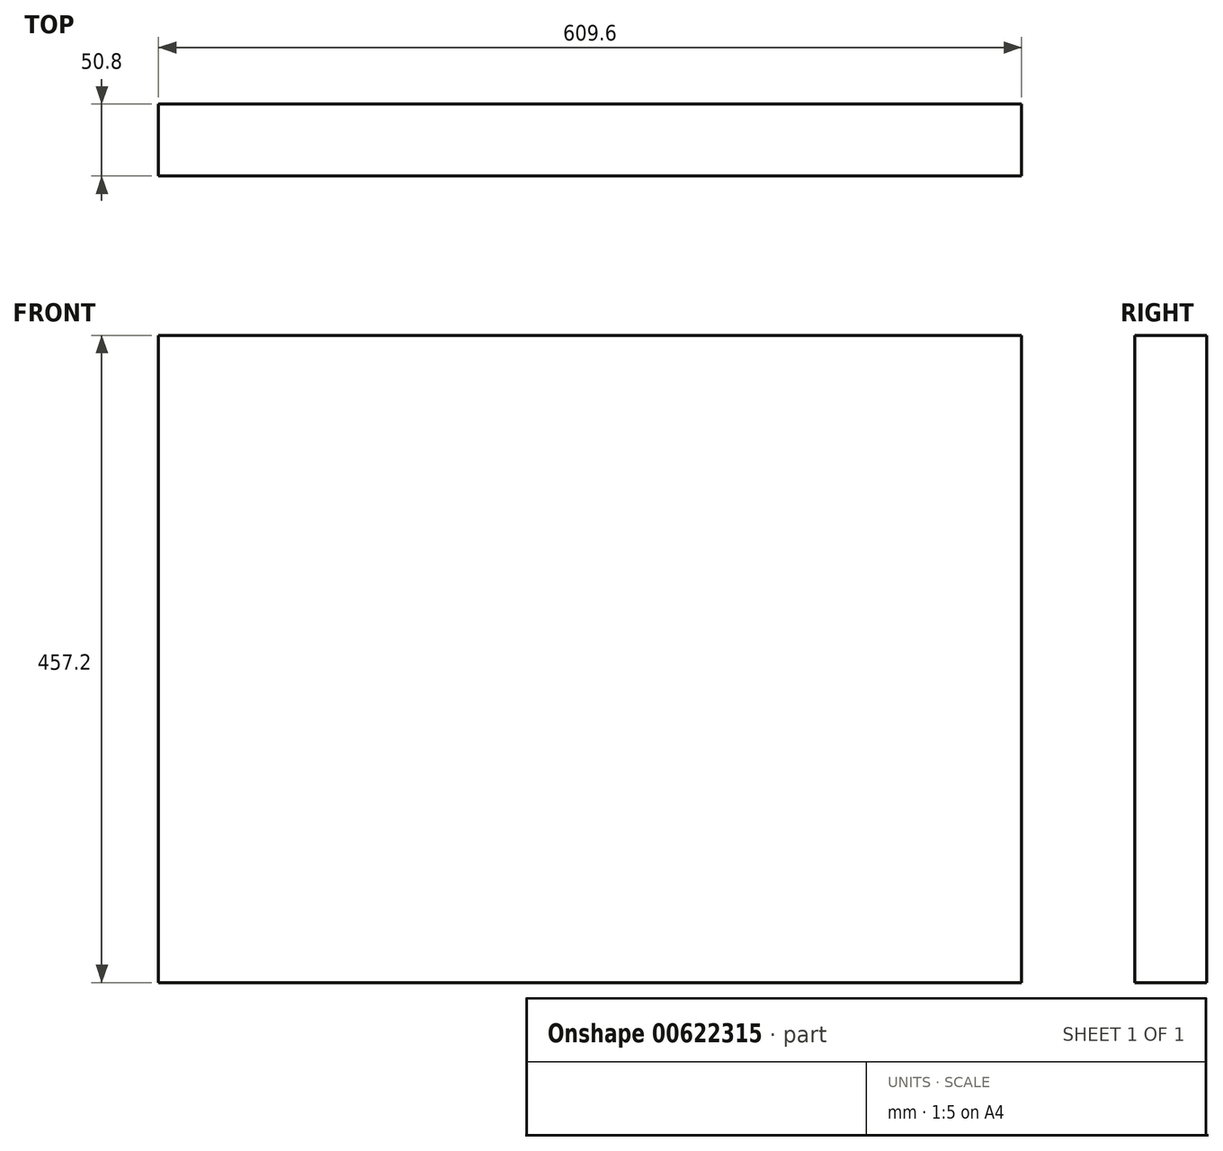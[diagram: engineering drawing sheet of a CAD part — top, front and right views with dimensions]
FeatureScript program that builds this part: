
annotation { "Feature Type Name" : "Feature", "Feature Type Description" : "" }
export const myFeature = defineFeature(function(context is Context, id is Id, definition is map)
    precondition{}
    {
        {
            var Q0;
            Q0=qCreatedBy(makeId("Front.planeOp"),FACE);
            var sketch = newSketch(context, id + "F0", { "sketchPlane" : qUnion([Q0])});
            skLineSegment(sketch, "E0.bottom", {"start": v(-303.86, -220.03) * mm, "end": v(305.74, -220.03) * mm});
            skLineSegment(sketch, "E0.top", {"start": v(-303.86, 237.17) * mm, "end": v(305.74, 237.17) * mm});
            skLineSegment(sketch, "E0.left", {"start": v(-303.86, -220.03) * mm, "end": v(-303.86, 237.17) * mm});
            skLineSegment(sketch, "E0.right", {"start": v(305.74, -220.03) * mm, "end": v(305.74, 237.17) * mm});
            skSolve(sketch);
        }
        {
            var Q0;
            Q0 = qSketchRegion(id + "F0", true);
            extrude(context, id + "F1", {"entities" : qUnion([Q0]), "depth" : 50.8 * mm, "offsetDistance" : 25.4 * mm});
        }
    });
